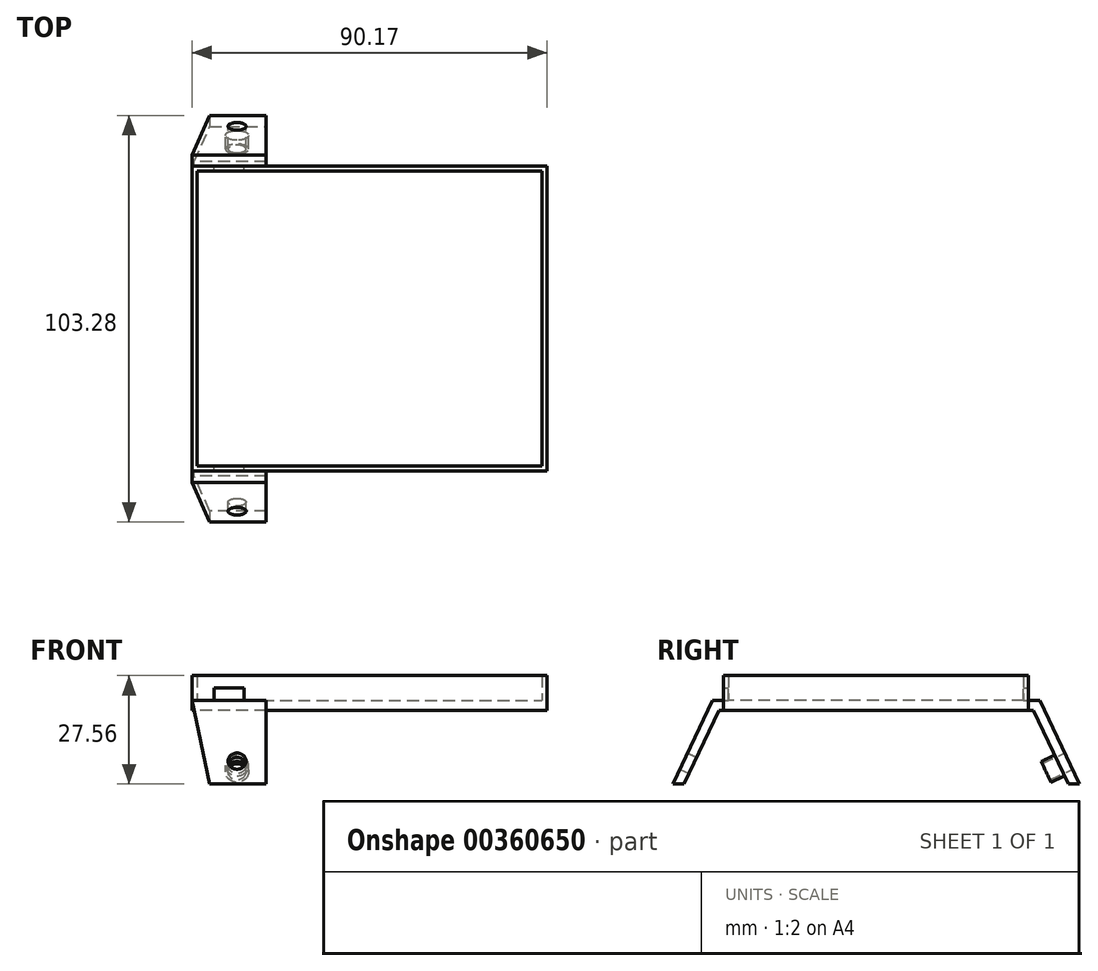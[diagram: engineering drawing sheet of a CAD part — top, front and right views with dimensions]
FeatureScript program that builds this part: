
annotation { "Feature Type Name" : "Feature", "Feature Type Description" : "" }
export const myFeature = defineFeature(function(context is Context, id is Id, definition is map)
    precondition{}
    {
        {
            var Q0;
            Q0=qCreatedBy(makeId("Right.planeOp"),FACE);
            var sketch = newSketch(context, id + "F0", { "sketchPlane" : qUnion([Q0])});
            skLineSegment(sketch, "E0.0", {"start": v(-39.57, 10.61) * mm, "end": v(-53.34, -18.4) * mm, "construction": true});
            skLineSegment(sketch, "E0.1", {"start": v(-37.96, 8.07) * mm, "end": v(-50.8, -18.97) * mm, "construction": true});
            skLineSegment(sketch, "E0.2", {"start": v(37.96, 8.07) * mm, "end": v(-37.96, 8.07) * mm, "construction": true});
            skLineSegment(sketch, "E0.3", {"start": v(39.57, 10.61) * mm, "end": v(-39.57, 10.61) * mm, "construction": true});
            skLineSegment(sketch, "E0.4", {"start": v(50.8, -18.97) * mm, "end": v(37.96, 8.07) * mm, "construction": true});
            skLineSegment(sketch, "E0.5", {"start": v(53.34, -18.4) * mm, "end": v(39.57, 10.61) * mm, "construction": true});
            skLineSegment(sketch, "E1", {"start": v(-53.34, -18.4) * mm, "end": v(-50.8, -18.97) * mm, "construction": true});
            skLineSegment(sketch, "E2", {"start": v(50.8, -18.97) * mm, "end": v(53.34, -18.4) * mm, "construction": true});
            skPoint(sketch, "E3", {"position": v(-46.46, -3.9) * mm});
            skPoint(sketch, "E4", {"position": v(46.46, -3.9) * mm});
            skLineSegment(sketch, "E5.0", {"start": v(-39.97, 11.25) * mm, "end": v(-53.91, -18.13) * mm});
            skLineSegment(sketch, "E5.1", {"start": v(39.97, 11.25) * mm, "end": v(-39.97, 11.25) * mm});
            skLineSegment(sketch, "E5.2", {"start": v(53.91, -18.13) * mm, "end": v(39.97, 11.25) * mm});
            skLineSegment(sketch, "E6.0", {"start": v(-41.58, 13.79) * mm, "end": v(-56.2, -17.04) * mm});
            skLineSegment(sketch, "E6.1", {"start": v(41.58, 13.79) * mm, "end": v(-41.58, 13.79) * mm});
            skLineSegment(sketch, "E6.2", {"start": v(56.2, -17.04) * mm, "end": v(41.58, 13.79) * mm});
            skLineSegment(sketch, "E7", {"start": v(-56.2, -17.04) * mm, "end": v(-53.91, -18.13) * mm});
            skLineSegment(sketch, "E8", {"start": v(53.91, -18.13) * mm, "end": v(56.2, -17.04) * mm});
            skSolve(sketch);
        }
        {
            var Q0;
            Q0 = qSketchRegion(id + "F0", true);
            extrude(context, id + "F1", {"entities" : qUnion([Q0]), "depth" : 31.75 * mm, "offsetDistance" : 25.4 * mm});
        }
        {
            var Q0;
            Q0=qCreatedBy(makeId("Front.planeOp"),FACE);
            var sketch = newSketch(context, id + "F2", { "sketchPlane" : qUnion([Q0])});
            skLineSegment(sketch, "E9", {"start": v(0, 13.79) * mm, "end": v(12.9, 13.79) * mm});
            skLineSegment(sketch, "E10", {"start": v(12.9, 13.79) * mm, "end": v(17.4, -7.42) * mm});
            skLineSegment(sketch, "E11", {"start": v(19.67, -18.13) * mm, "end": v(0, -18.13) * mm});
            skLineSegment(sketch, "E12", {"start": v(0, -18.13) * mm, "end": v(0, 13.79) * mm});
            skLineSegment(sketch, "E13", {"start": v(17.4, -7.42) * mm, "end": v(35.76, -7.42) * mm});
            skLineSegment(sketch, "E14", {"start": v(35.76, -7.42) * mm, "end": v(35.76, -19.07) * mm});
            skLineSegment(sketch, "E15", {"start": v(35.76, -19.07) * mm, "end": v(19.67, -18.13) * mm});
            skPoint(sketch, "E16", {"position": v(31.75, -1.62) * mm});
            skCircle(sketch, "E17", {"center": v(24.33, -1.62) * mm, "radius": 0.13 * mm});
            skSolve(sketch);
        }
        {
            var Q0;
            Q0=makeQuery(id+"F2.imprint","IMPRINT",FACE,{"disambiguationData":[TD([[makeQuery(id+"F2.imprint","IMPRINT",EDGE,{"derivedFrom":sQuery(id+"F2.wireOp",EDGE,"E9")}),-1.0]])]});
            var Q1;
            Q1=makeQuery(id+"F2.imprint","IMPRINT",FACE,{"disambiguationData":[TD([[makeQuery(id+"F2.imprint","IMPRINT",EDGE,{"derivedFrom":sQuery(id+"F2.wireOp",EDGE,"E17")}),1.0]])]});
            extrude(context, id + "F3", {"entities" : qUnion([Q0, Q1]), "operationType" : NewBodyOperationType.REMOVE, "endBound" : BoundingType.THROUGH_ALL, "oppositeDirection" : true, "depth" : 25.4 * mm, "offsetDistance" : 25.4 * mm, "hasSecondDirection" : true, "secondDirectionBound" : SecondDirectionBoundingType.THROUGH_ALL, "secondDirectionOppositeDirection" : false, "secondDirectionDepth" : 25.4 * mm});
        }
        {
            var Q0;
            Q0=makeQuery(id+"F1.opExtrude","SWEPT_FACE",FACE,{"disambiguationData":[OSD([sQuery(id+"F0.wireOp",EDGE,"E5.1")])]});
            var sketch = newSketch(context, id + "F4", { "sketchPlane" : qUnion([Q0])});
            skLineSegment(sketch, "E18.bottom", {"start": v(103.07, -38.74) * mm, "end": v(12.9, -38.73) * mm});
            skLineSegment(sketch, "E18.top", {"start": v(103.07, 38.74) * mm, "end": v(12.9, 38.73) * mm});
            skLineSegment(sketch, "E18.left", {"start": v(103.07, -38.73) * mm, "end": v(103.07, 38.73) * mm});
            skLineSegment(sketch, "E18.right", {"start": v(12.9, -38.73) * mm, "end": v(12.9, 38.73) * mm});
            skPoint(sketch, "E19", {"position": v(103.07, 0) * mm});
            skSolve(sketch);
        }
        {
            var Q0;
            Q0 = qSketchRegion(id + "F4", true);
            var Q1;
            Q1=makeQuery(id+"F1.opExtrude","SWEPT_FACE",FACE,{"disambiguationData":[OSD([sQuery(id+"F0.wireOp",EDGE,"E6.1")])]});
            extrude(context, id + "F5", {"entities" : qUnion([Q0]), "operationType" : NewBodyOperationType.ADD, "endBound" : BoundingType.UP_TO_SURFACE, "oppositeDirection" : true, "depth" : 25.4 * mm, "endBoundEntityFace" : qUnion([Q1]), "offsetDistance" : 25.4 * mm});
        }
        {
            var Q0;
            Q0=makeQuery(id+"F5.boolean.opBoolean","MERGE",FACE,{"derivedFrom":[makeQuery(id+"F1.opExtrude","SWEPT_FACE",FACE,{"disambiguationData":[OSD([sQuery(id+"F0.wireOp",EDGE,"E6.1")])]}),makeQuery(id+"F5.opExtrude","CAP_FACE",FACE,{"disambiguationData":[OSD([sQuery(id+"F4.wireOp",EDGE,"E18.bottom"),sQuery(id+"F4.wireOp",EDGE,"E18.top"),sQuery(id+"F4.wireOp",EDGE,"E18.left"),sQuery(id+"F4.wireOp",EDGE,"E18.right")])],"isStart":false})]});
            var sketch = newSketch(context, id + "F6", { "sketchPlane" : qUnion([Q0])});
            skLineSegment(sketch, "E20.bottom", {"start": v(14.17, 37.46) * mm, "end": v(101.8, 37.46) * mm});
            skLineSegment(sketch, "E20.top", {"start": v(14.17, -37.46) * mm, "end": v(101.8, -37.46) * mm});
            skLineSegment(sketch, "E20.left", {"start": v(14.17, 37.46) * mm, "end": v(14.17, -37.46) * mm});
            skLineSegment(sketch, "E20.right", {"start": v(101.8, 37.46) * mm, "end": v(101.8, -37.46) * mm});
            skLineSegment(sketch, "E21.0", {"start": v(12.9, 38.73) * mm, "end": v(103.07, 38.73) * mm});
            skLineSegment(sketch, "E21.1", {"start": v(12.9, 38.73) * mm, "end": v(12.9, -38.73) * mm});
            skLineSegment(sketch, "E21.2", {"start": v(12.9, -38.73) * mm, "end": v(103.07, -38.73) * mm});
            skLineSegment(sketch, "E21.3", {"start": v(103.07, 38.73) * mm, "end": v(103.07, -38.73) * mm});
            skSolve(sketch);
        }
        {
            var Q0;
            Q0 = qSketchRegion(id + "F6", true);
            extrude(context, id + "F7", {"entities" : qUnion([Q0]), "operationType" : NewBodyOperationType.ADD, "depth" : 6.35 * mm, "offsetDistance" : 25.4 * mm});
        }
        {
            var Q0;
            Q0=makeQuery(id+"F7.boolean.opBoolean","MERGE",FACE,{"derivedFrom":[makeQuery(id+"F5.opExtrude","SWEPT_FACE",FACE,{"disambiguationData":[OSD([sQuery(id+"F4.wireOp",EDGE,"E18.left")])]}),makeQuery(id+"F7.opExtrude","SWEPT_FACE",FACE,{"disambiguationData":[OSD([sQuery(id+"F6.wireOp",EDGE,"E21.3")])]})]});
            var sketch = newSketch(context, id + "F8", { "sketchPlane" : qUnion([Q0])});
            skLineSegment(sketch, "E22.bottom", {"start": v(-3.18, 17.28) * mm, "end": v(3.18, 17.28) * mm});
            skLineSegment(sketch, "E22.top", {"start": v(-3.18, 14.1) * mm, "end": v(3.18, 14.1) * mm});
            skLineSegment(sketch, "E22.left", {"start": v(-3.18, 17.28) * mm, "end": v(-3.18, 14.1) * mm});
            skLineSegment(sketch, "E22.right", {"start": v(3.17, 17.28) * mm, "end": v(3.17, 14.1) * mm});
            skPoint(sketch, "E23", {"position": v(0, 17.28) * mm});
            skPoint(sketch, "E24", {"position": v(-38.73, 15.7) * mm});
            skPoint(sketch, "E25", {"position": v(-3.18, 15.7) * mm});
            skSolve(sketch);
        }
        {
            var Q0;
            Q0=makeQuery(id+"F1.opExtrude","SWEPT_FACE",FACE,{"disambiguationData":[OSD([sQuery(id+"F0.wireOp",EDGE,"E6.2")])]});
            var sketch = newSketch(context, id + "F9", { "sketchPlane" : qUnion([Q0])});
            skLineSegment(sketch, "E26", {"start": v(-24.57, -28.85) * mm, "end": v(-23.68, -5.37) * mm, "construction": true});
            skPoint(sketch, "E27", {"position": v(-24.33, -22.43) * mm});
            skSolve(sketch);
        }
        {
            var Q0;
            Q0=makeQuery(id+"F1.opExtrude","SWEPT_FACE",FACE,{"disambiguationData":[OSD([sQuery(id+"F0.wireOp",EDGE,"E6.0")])]});
            var sketch = newSketch(context, id + "F10", { "sketchPlane" : qUnion([Q0])});
            skLineSegment(sketch, "E28", {"start": v(17.44, -5.37) * mm, "end": v(21.94, -28.85) * mm});
            skPoint(sketch, "E29", {"position": v(24.33, -22.43) * mm});
            skLineSegment(sketch, "E30", {"start": v(21.94, -28.85) * mm, "end": v(29.18, -28.85) * mm});
            skLineSegment(sketch, "E31", {"start": v(29.18, -28.85) * mm, "end": v(24.68, -5.37) * mm});
            skLineSegment(sketch, "E32.1", {"start": v(18.09, -5.37) * mm, "end": v(22.46, -28.21) * mm});
            skLineSegment(sketch, "E32.2", {"start": v(22.46, -28.21) * mm, "end": v(28.41, -28.21) * mm});
            skLineSegment(sketch, "E33", {"start": v(17.44, -5.37) * mm, "end": v(18.09, -5.37) * mm});
            skLineSegment(sketch, "E34", {"start": v(24.07, -5.37) * mm, "end": v(24.68, -5.37) * mm});
            skLineSegment(sketch, "E35", {"start": v(24.07, -5.37) * mm, "end": v(28.41, -28.21) * mm});
            skSolve(sketch);
        }
        {
            var Q0;
            {var subQ1=sQuery(id+"F4.wireOp",EDGE,"E18.left");var subQ3=sQuery(id+"F4.wireOp",EDGE,"E18.bottom");Q0=makeQuery(id+"F7.boolean.opBoolean","MERGE",FACE,{"derivedFrom":[makeQuery(id+"F5.boolean.opBoolean","SPLIT",FACE,{"disambiguationData":[TD([makeQuery(id+"F5.opExtrude","SWEPT_FACE",FACE,{"disambiguationData":[OSD([subQ1])]})])],"derivedFrom":makeQuery(id+"F5.opExtrude","SWEPT_FACE",FACE,{"disambiguationData":[OSD([subQ3])]})}),makeQuery(id+"F7.opExtrude","SWEPT_FACE",FACE,{"disambiguationData":[OSD([sQuery(id+"F6.wireOp",EDGE,"E21.0")])]})]});}
            var sketch = newSketch(context, id + "F11", { "sketchPlane" : qUnion([Q0])});
            skLineSegment(sketch, "E36.bottom", {"start": v(-26.13, 13.79) * mm, "end": v(-18.51, 13.79) * mm});
            skLineSegment(sketch, "E36.top", {"start": v(-26.13, 16.96) * mm, "end": v(-18.51, 16.96) * mm});
            skLineSegment(sketch, "E36.left", {"start": v(-26.13, 13.79) * mm, "end": v(-26.13, 16.96) * mm});
            skLineSegment(sketch, "E36.right", {"start": v(-18.51, 13.79) * mm, "end": v(-18.51, 16.96) * mm});
            skPoint(sketch, "E37", {"position": v(-22.32, 13.79) * mm});
            skPoint(sketch, "E38", {"position": v(-22.32, 16.96) * mm});
            skSolve(sketch);
        }
        {
            var Q0;
            Q0 = qSketchRegion(id + "F11", true);
            extrude(context, id + "F12", {"entities" : qUnion([Q0]), "operationType" : NewBodyOperationType.REMOVE, "oppositeDirection" : true, "depth" : 79.76 * mm, "offsetDistance" : 25.4 * mm});
        }
        {
            var Q0;
            Q0=makeQuery(id+"F1.opExtrude","SWEPT_FACE",FACE,{"disambiguationData":[OSD([sQuery(id+"F0.wireOp",EDGE,"E5.0")])]});
            var sketch = newSketch(context, id + "F13", { "sketchPlane" : qUnion([Q0])});
            skCircle(sketch, "E39", {"center": v(-24.33, -21.23) * mm, "radius": 2.29 * mm});
            skCircle(sketch, "E40", {"center": v(-24.33, -21.23) * mm, "radius": 2.92 * mm});
            skCircle(sketch, "E41", {"center": v(-24.33, -21.23) * mm, "radius": 5.12 * mm});
            skSolve(sketch);
        }
        {
            var Q0;
            Q0=makeQuery(id+"F1.opExtrude","SWEPT_FACE",FACE,{"disambiguationData":[OSD([sQuery(id+"F0.wireOp",EDGE,"E6.2")])]});
            var sketch = newSketch(context, id + "F14", { "sketchPlane" : qUnion([Q0])});
            skCircle(sketch, "E42", {"center": v(-24.33, -22.43) * mm, "radius": 2.29 * mm});
            skCircle(sketch, "E43", {"center": v(-24.33, -22.43) * mm, "radius": 2.92 * mm});
            skSolve(sketch);
        }
        {
            var Q0;
            Q0 = qSketchRegion(id + "F14", true);
            extrude(context, id + "F15", {"entities" : qUnion([Q0]), "operationType" : NewBodyOperationType.ADD, "oppositeDirection" : true, "depth" : 6.35 * mm, "offsetDistance" : 25.4 * mm});
        }
        {
            var Q0;
            Q0 = qSketchRegion(id + "F14", true);
            var Q1;
            {var subQ0=makeQuery(id+"F1.opExtrude","SWEPT_FACE",FACE,{"disambiguationData":[OSD([sQuery(id+"F0.wireOp",EDGE,"E5.2")])]});Q1=makeQuery(id+"F15.boolean.opBoolean","SPLIT",FACE,{"disambiguationData":[TD([makeQuery(id+"F15.opExtrude","SWEPT_FACE",FACE,{"disambiguationData":[OSD([sQuery(id+"F14.wireOp",EDGE,"E42")])]})])],"derivedFrom":subQ0});}
            extrude(context, id + "F16", {"entities" : qUnion([Q0, Q1]), "operationType" : NewBodyOperationType.REMOVE, "depth" : 12.93 * mm, "offsetDistance" : 25.4 * mm});
        }
        {
            var Q0;
            Q0=makeQuery(id+"F15.opExtrude","CAP_FACE",FACE,{"disambiguationData":[OSD([sQuery(id+"F14.wireOp",EDGE,"E42"),sQuery(id+"F14.wireOp",EDGE,"E43")])],"isStart":false});
            var sketch = newSketch(context, id + "F17", { "sketchPlane" : qUnion([Q0])});
            skCircle(sketch, "E44", {"center": v(24.33, -22.43) * mm, "radius": 2.07 * mm});
            skSolve(sketch);
        }
        {
            var Q0;
            Q0 = qSketchRegion(id + "F17", true);
            extrude(context, id + "F18", {"entities" : qUnion([Q0]), "operationType" : NewBodyOperationType.REMOVE, "oppositeDirection" : true, "depth" : 25.4 * mm, "offsetDistance" : 25.4 * mm});
        }
        {
            var Q0;
            {var subQ1=sQuery(id+"F4.wireOp",EDGE,"E18.left");var subQ3=sQuery(id+"F4.wireOp",EDGE,"E18.bottom");Q0=makeQuery(id+"F7.boolean.opBoolean","MERGE",FACE,{"derivedFrom":[makeQuery(id+"F5.boolean.opBoolean","SPLIT",FACE,{"disambiguationData":[TD([makeQuery(id+"F5.opExtrude","SWEPT_FACE",FACE,{"disambiguationData":[OSD([subQ1])]})])],"derivedFrom":makeQuery(id+"F5.opExtrude","SWEPT_FACE",FACE,{"disambiguationData":[OSD([subQ3])]})}),makeQuery(id+"F7.opExtrude","SWEPT_FACE",FACE,{"disambiguationData":[OSD([sQuery(id+"F6.wireOp",EDGE,"E21.0")])]})]});}
            var Q1;
            {var subQ1=sQuery(id+"F4.wireOp",EDGE,"E18.left");var subQ2=sQuery(id+"F4.wireOp",EDGE,"E18.top");Q1=makeQuery(id+"F7.boolean.opBoolean","MERGE",FACE,{"derivedFrom":[makeQuery(id+"F5.boolean.opBoolean","SPLIT",FACE,{"disambiguationData":[TD([makeQuery(id+"F5.opExtrude","SWEPT_FACE",FACE,{"disambiguationData":[OSD([subQ1])]})])],"derivedFrom":makeQuery(id+"F5.opExtrude","SWEPT_FACE",FACE,{"disambiguationData":[OSD([subQ2])]})}),makeQuery(id+"F7.opExtrude","SWEPT_FACE",FACE,{"disambiguationData":[OSD([sQuery(id+"F6.wireOp",EDGE,"E21.2")])]})]});}
            cPlane(context, id + "F19", {"entities" : qUnion([Q0, Q1]), "cplaneType" : CPlaneType.MID_PLANE, "offset" : 25.4 * mm, "width" : 152.4 * mm, "height" : 152.4 * mm});
        }
        {
            var Q0;
            Q0=makeQuery(id+"F13.imprint","IMPRINT",FACE,{"disambiguationData":[TD([[makeQuery(id+"F13.imprint","IMPRINT",EDGE,{"derivedFrom":sQuery(id+"F13.wireOp",EDGE,"E41")}),-1.0]])]});
            var sketch = newSketch(context, id + "F20", { "sketchPlane" : qUnion([Q0])});
            skCircle(sketch, "E45", {"center": v(-24.33, -22.43) * mm, "radius": 2.29 * mm});
            skSolve(sketch);
        }
        {
            var Q0;
            Q0 = qSketchRegion(id + "F20", true);
            extrude(context, id + "F21", {"entities" : qUnion([Q0]), "operationType" : NewBodyOperationType.REMOVE, "oppositeDirection" : true, "depth" : 25.4 * mm, "offsetDistance" : 25.4 * mm});
        }
    });
